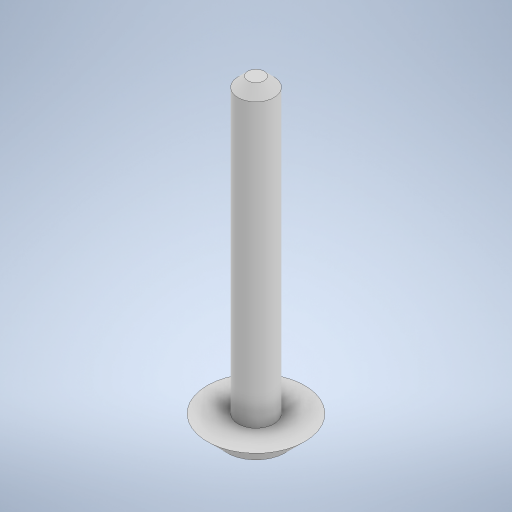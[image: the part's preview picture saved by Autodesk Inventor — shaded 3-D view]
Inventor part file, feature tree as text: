
AUTODESK INVENTOR PART (.ipt)
format: ipt  version: 2023 (Build 270158000, 158)  size: 240,128 bytes
history: native  units: mm
features: extrude x2, chamfer x2, sketch x2
ambient origin geometry x8: Origin, YZ Plane, XZ Plane, XY Plane, X Axis, Y Axis, Z Axis, Center Point
bodies: Solid1 (feature_tree)
feature tree (6):
  extrude  "Extrusion1"  Depth=30.0mm TaperAngle=0.0deg
  extrude  "Extrusion2"  Depth=2.0mm TaperAngle=0.0deg
  chamfer  "Chamfer1"  Distance=1.0mm Angle=45.0deg
  chamfer  "Chamfer2"  Distance=2.0mm Angle=45.0deg
  sketch  "Sketch1"  dims[d0=3.7mm d1=30.0mm d2=0.0mm]
  sketch  "Sketch2"  dims[d3=10.0mm d4=2.0mm d5=0.0mm d6=1.0mm d7=2.0mm d8=45.0deg d9=2.0mm d10=2.0mm d11=45.0deg]
